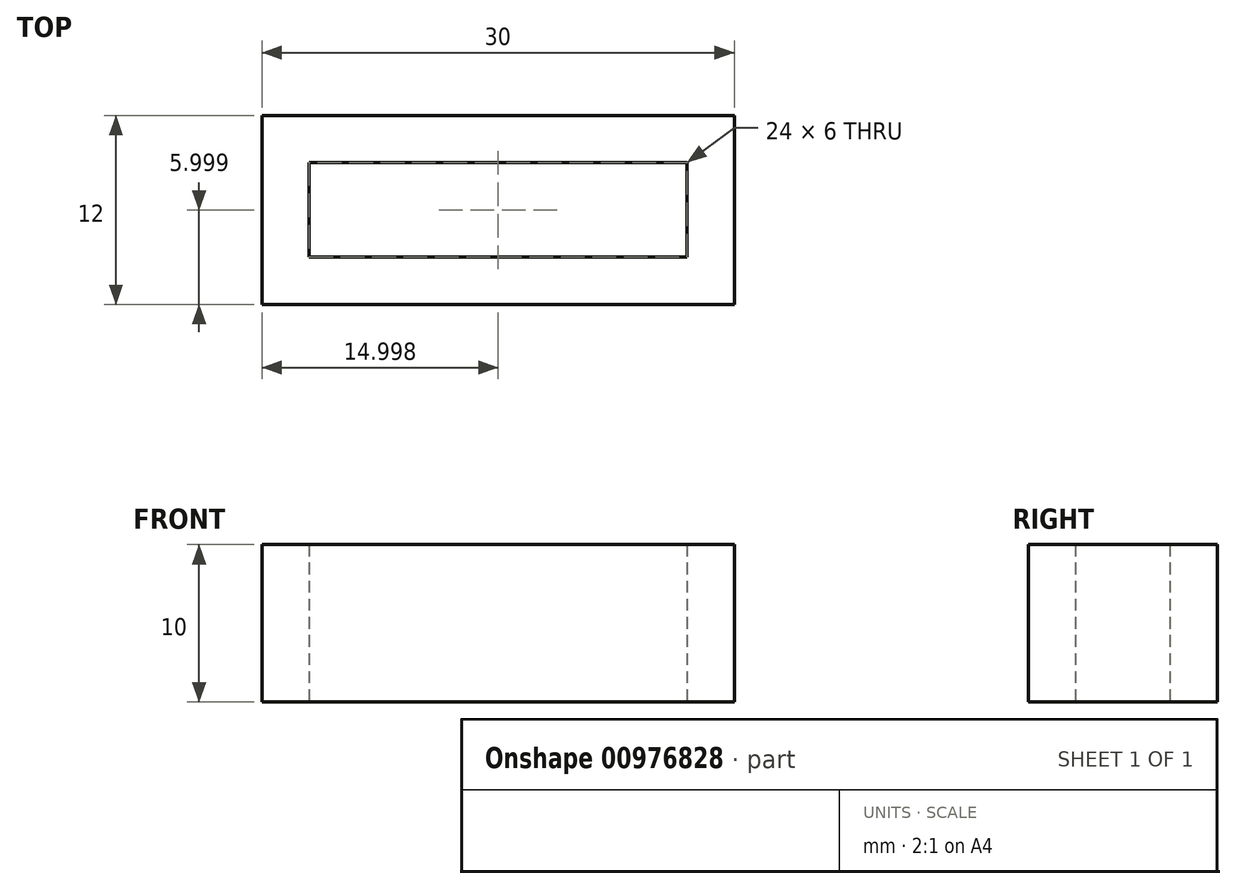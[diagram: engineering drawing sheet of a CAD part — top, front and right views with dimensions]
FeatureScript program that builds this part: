
annotation { "Feature Type Name" : "Feature", "Feature Type Description" : "" }
export const myFeature = defineFeature(function(context is Context, id is Id, definition is map)
    precondition{}
    {
        {
            var Q0;
            Q0=qCreatedBy(makeId("Top.planeOp"),FACE);
            var sketch = newSketch(context, id + "F0", { "sketchPlane" : qUnion([Q0])});
            skLineSegment(sketch, "E0.bottom", {"start": v(-8.57, 9.97) * mm, "end": v(21.43, 9.97) * mm});
            skLineSegment(sketch, "E0.top", {"start": v(-8.57, -2.03) * mm, "end": v(21.43, -2.03) * mm});
            skLineSegment(sketch, "E0.left", {"start": v(-8.57, 9.97) * mm, "end": v(-8.57, -2.03) * mm});
            skLineSegment(sketch, "E0.right", {"start": v(21.43, 9.97) * mm, "end": v(21.43, -2.03) * mm});
            skLineSegment(sketch, "E1", {"start": v(-8.57, 9.97) * mm, "end": v(21.43, -2.03) * mm});
            skLineSegment(sketch, "E2", {"start": v(21.43, 9.97) * mm, "end": v(-8.57, -2.03) * mm});
            skLineSegment(sketch, "E3.bottom", {"start": v(18.43, 6.97) * mm, "end": v(-5.57, 6.97) * mm});
            skLineSegment(sketch, "E3.top", {"start": v(18.43, 0.97) * mm, "end": v(-5.57, 0.97) * mm});
            skLineSegment(sketch, "E3.left", {"start": v(18.43, 6.97) * mm, "end": v(18.43, 0.97) * mm});
            skLineSegment(sketch, "E3.right", {"start": v(-5.57, 6.97) * mm, "end": v(-5.57, 0.97) * mm});
            skPoint(sketch, "E3.middle", {"position": v(6.43, 3.97) * mm});
            skSolve(sketch);
        }
        {
            var Q0;
            Q0 = qSketchRegion(id + "F0", true);
            extrude(context, id + "F1", {"entities" : qUnion([Q0]), "depth" : 10 * mm, "offsetDistance" : 25.4 * mm});
        }
    });
